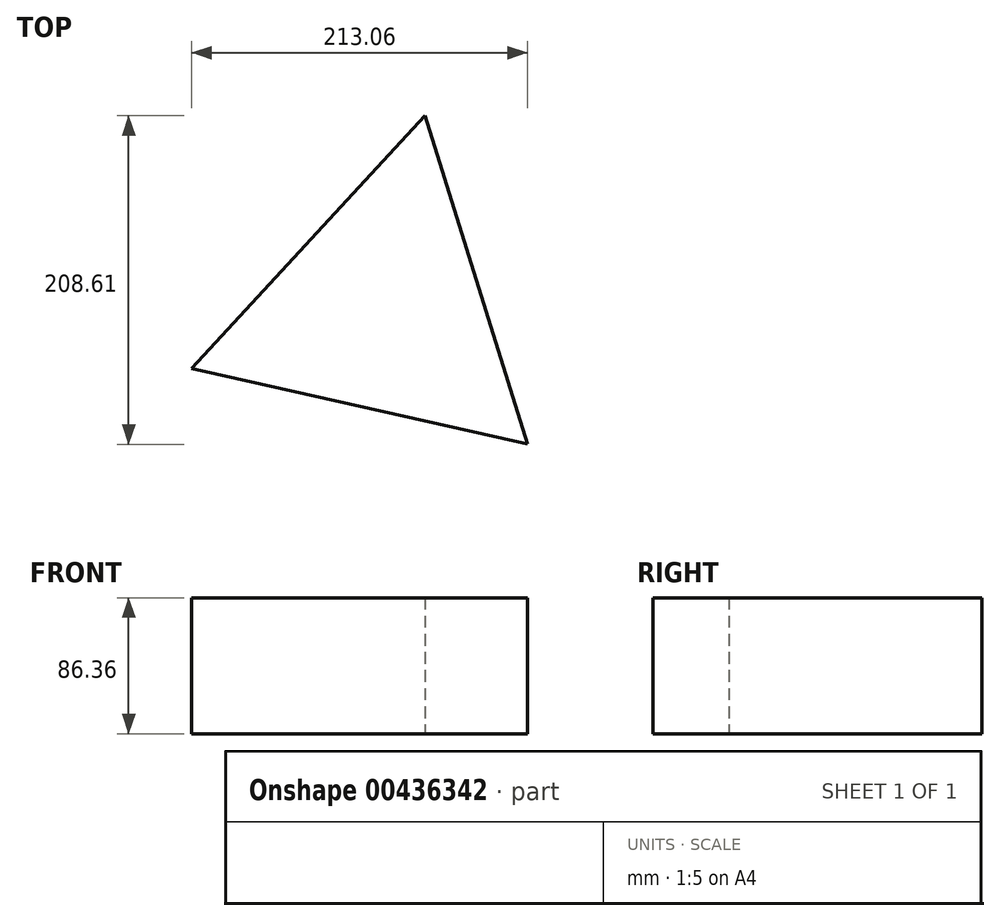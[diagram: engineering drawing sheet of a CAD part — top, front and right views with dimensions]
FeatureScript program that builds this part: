
annotation { "Feature Type Name" : "Feature", "Feature Type Description" : "" }
export const myFeature = defineFeature(function(context is Context, id is Id, definition is map)
    precondition{}
    {
        {
            var Q0;
            Q0=qCreatedBy(makeId("Top.planeOp"),FACE);
            var sketch = newSketch(context, id + "F0", { "sketchPlane" : qUnion([Q0])});
            skLineSegment(sketch, "E0", {"start": v(-148.26, -62.33) * mm, "end": v(0, 98.1) * mm});
            skLineSegment(sketch, "E1", {"start": v(0, 98.1) * mm, "end": v(64.8, -110.52) * mm});
            skLineSegment(sketch, "E2", {"start": v(64.8, -110.52) * mm, "end": v(-148.26, -62.33) * mm});
            skSolve(sketch);
        }
        {
            var Q0;
            Q0=makeQuery(id+"F0.imprint","IMPRINT",FACE,{"disambiguationData":[TD([[makeQuery(id+"F0.imprint","IMPRINT",EDGE,{"derivedFrom":sQuery(id+"F0.wireOp",EDGE,"E0")}),-1.0]])]});
            extrude(context, id + "F1", {"entities" : qUnion([Q0]), "depth" : 86.36 * mm});
        }
    });
